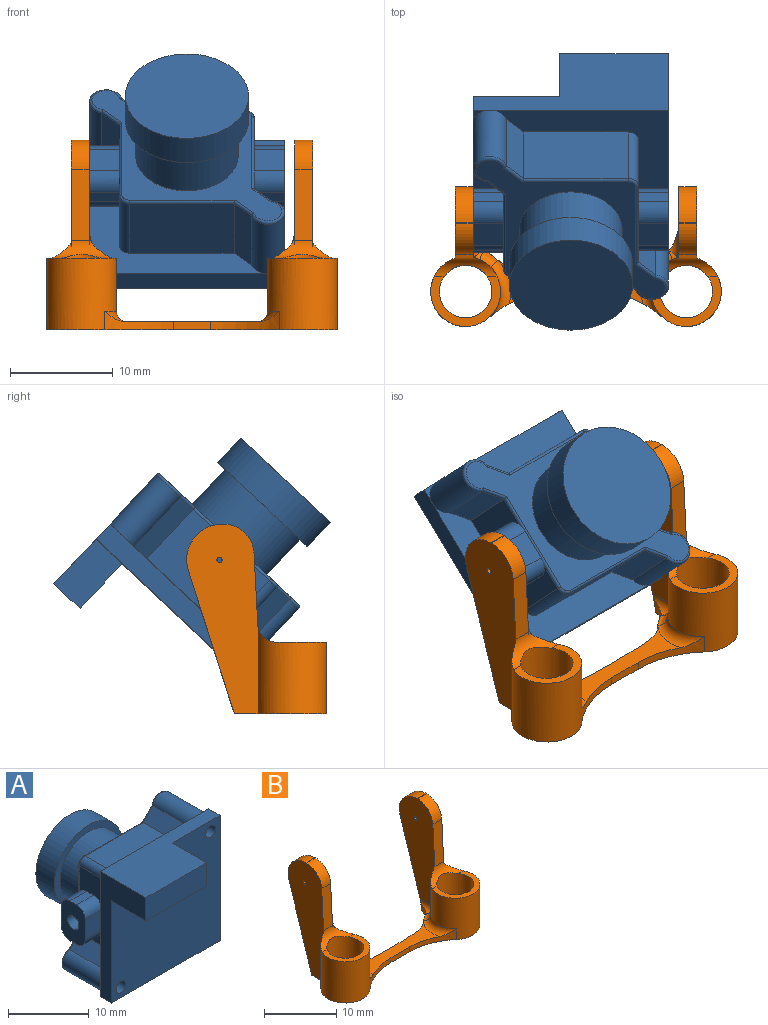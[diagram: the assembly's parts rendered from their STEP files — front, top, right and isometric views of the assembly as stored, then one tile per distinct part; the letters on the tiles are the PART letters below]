
ASSEMBLY  parts=2 mates=1
PART A: 69 faces, bbox 19.3x22.8x19.3 mm
  f0: plane 17.38x17.38mm, normal (0,1,0), area 82.2mm2, adj f3,f4,f43,f59,f60,f61,f62,f63
  f1: plane 1.63x1.63mm, normal (0,1,0), area 0.6mm2, adj f3,f8,f63
  f2: plane 1.63x1.63mm, normal (0,1,0), area 0.6mm2, adj f4,f5,f59
  f3: plane 19x2mm, normal (1,0,0), area 38mm2, adj f0,f1,f4,f8,f10
  f4: plane 19x2mm, normal (0,0,-1), area 38mm2, adj f0,f2,f3,f5,f10
  f5: plane 19x8mm, normal (-1,0,0), area 59mm2, adj f2,f4,f8,f9,f10,f12,f13
  f6: cylinder r=0.88mm len=2mm, axis (0,-1,0), area 11mm2, adj f10,f67
  f7: cylinder r=0.88mm len=2mm, axis (0,-1,0), area 11mm2, adj f10,f68
  f8: plane 19x8mm, normal (0,0,1), area 101.6mm2, adj f1,f3,f5,f9,f10,f11,f13
  f9: plane 17.38x17.38mm, normal (0,1,0), area 82.2mm2, adj f5,f8,f45,f56,f57,f58,f59,f63
  f10: plane 19x19mm, normal (0,-1,0), area 319.1mm2, adj f3,f4,f5,f6,f7,f8,f11,f12
  f11: plane 6x3.5mm, normal (1,0,0), area 21mm2, adj f8,f10,f12,f13
  f12: plane 10.6x6mm, normal (0,0,-1), area 63.6mm2, adj f5,f10,f11,f13
  f13: plane 10.6x3.5mm, normal (0,-1,0), area 37.1mm2, adj f5,f8,f11,f12
  f14: plane 2x2mm, normal (-1,0,0), area 3.1mm2, adj f19
  f15: cylinder r=1.5mm len=2.93mm, axis (-1,0,0), area 6.9mm2, adj f20,f21,f24,f57
  f16: cylinder r=1.5mm len=2.93mm, axis (-1,0,0), area 6.9mm2, adj f20,f22,f24,f25,f57
  f17: cylinder r=1.5mm len=2.93mm, axis (1,0,0), area 6.9mm2, adj f22,f23,f24,f25,f57
  f18: cylinder r=1.5mm len=2.93mm, axis (1,0,0), area 6.9mm2, adj f21,f23,f24,f57
  f19: cylinder r=1mm len=2.93mm, axis (1,0,0), area 18.4mm2, adj f14,f24
  f20: plane 2.93x1.2mm, normal (0,0,1), area 3.5mm2, adj f15,f16,f24,f57
  f21: plane 3x2.93mm, normal (0,-1,0), area 8.8mm2, adj f15,f18,f24,f57
  f22: plane 3x2.93mm, normal (0,1,0), area 8.8mm2, adj f16,f17,f24,f25
  f23: plane 2.93x1.2mm, normal (0,0,-1), area 3.5mm2, adj f17,f18,f24,f57
  f24: plane 6x4.2mm, normal (-1,0,0), area 20.1mm2, adj f15,f16,f17,f18,f19,f20,f21,f22
  f25: plane 4.66x0.25mm, normal (1,0,0), area 1mm2, adj f16,f17,f22,f52
  f26: plane 2x2mm, normal (1,0,0), area 3.1mm2, adj f31
  f27: cylinder r=1.5mm len=2.93mm, axis (1,0,0), area 6.9mm2, adj f32,f33,f36,f66
  f28: cylinder r=1.5mm len=2.93mm, axis (1,0,0), area 6.9mm2, adj f32,f34,f36,f37,f66
  f29: cylinder r=1.5mm len=2.93mm, axis (-1,0,0), area 6.9mm2, adj f34,f35,f36,f37,f66
  f30: cylinder r=1.5mm len=2.93mm, axis (-1,0,0), area 6.9mm2, adj f33,f35,f36,f66
  f31: cylinder r=1mm len=2.93mm, axis (-1,0,0), area 18.4mm2, adj f26,f36
  f32: plane 2.93x1.2mm, normal (0,0,1), area 3.5mm2, adj f27,f28,f36,f66
  f33: plane 3x2.93mm, normal (0,-1,0), area 8.8mm2, adj f27,f30,f36,f66
  f34: plane 3x2.93mm, normal (0,1,0), area 8.8mm2, adj f28,f29,f36,f37
  f35: plane 2.93x1.2mm, normal (0,0,-1), area 3.5mm2, adj f29,f30,f36,f66
  f36: plane 6x4.2mm, normal (1,0,0), area 20.1mm2, adj f27,f28,f29,f30,f31,f32,f33,f34
  f37: plane 4.66x0.25mm, normal (-1,0,0), area 1mm2, adj f28,f29,f34,f49
  f38: plane 12x12mm, normal (0,-1,0), area 34.6mm2, adj f40,f41
  f39: plane 12x12mm, normal (0,1,0), area 113.1mm2, adj f40
  f40: cylinder r=6mm len=12mm, axis (0,-1,0), area 121.8mm2, adj f38,f39
  f41: cylinder r=5mm len=10mm, axis (0,-1,0), area 148.3mm2, adj f38,f65
  f42: torus R=0.75mm, axis (0,1,0), area 0.6mm2, adj f43,f47,f49,f65
  f43: cylinder r=1mm len=6.6mm, axis (0,-1,0), area 10.4mm2, adj f0,f42,f61,f66
  f44: torus R=0.75mm, axis (0,1,0), area 0.6mm2, adj f45,f52,f54,f65
  f45: cylinder r=1mm len=6.6mm, axis (0,-1,0), area 10.4mm2, adj f9,f44,f56,f57
  f46: cylinder r=0.25mm len=2.01mm, axis (0.71,0,0.71), area 1mm2, adj f47,f48,f60,f65
  f47: cylinder r=0.25mm len=10.27mm, axis (1,0,0), area 4mm2, adj f42,f46,f61,f65
  f48: torus R=1.38mm, axis (0,1,0), area 2.6mm2, adj f46,f50,f59,f65
  f49: cylinder r=0.25mm len=10.27mm, axis (0,0,1), area 4mm2, adj f37,f42,f51,f65,f66
  f50: cylinder r=0.25mm len=2.01mm, axis (-0.71,0,-0.71), area 1mm2, adj f48,f52,f58,f65
  f51: cylinder r=0.25mm len=2.01mm, axis (0.71,0,0.71), area 1mm2, adj f49,f53,f62,f65
  f52: cylinder r=0.25mm len=10.27mm, axis (0,0,-1), area 4mm2, adj f25,f44,f50,f57,f65
  f53: torus R=1.38mm, axis (0,1,0), area 2.6mm2, adj f51,f55,f63,f65
  f54: cylinder r=0.25mm len=10.27mm, axis (-1,0,0), area 4mm2, adj f44,f55,f56,f65
  f55: cylinder r=0.25mm len=2.01mm, axis (-0.71,0,-0.71), area 1mm2, adj f53,f54,f64,f65
  f56: plane 10.17x6.6mm, normal (0,0,1), area 67.1mm2, adj f9,f45,f54,f64
  f57: plane 10.17x6.6mm, normal (-1,0,0), area 44.9mm2, adj f9,f15,f16,f17,f18,f20,f21,f23
  f58: plane 6.6x1.71mm, normal (-0.71,0,0.71), area 15.9mm2, adj f9,f50,f57,f59
  f59: cylinder r=1.62mm len=6.6mm, axis (0,-1,0), area 45.1mm2, adj f0,f2,f9,f48,f58,f60
  f60: plane 6.6x1.71mm, normal (0.71,0,-0.71), area 15.9mm2, adj f0,f46,f59,f61
  f61: plane 10.17x6.6mm, normal (0,0,-1), area 67.1mm2, adj f0,f43,f47,f60
  f62: plane 6.6x1.71mm, normal (0.71,0,-0.71), area 15.9mm2, adj f0,f51,f63,f66
  f63: cylinder r=1.62mm len=6.6mm, axis (0,-1,0), area 45.1mm2, adj f0,f1,f9,f53,f62,f64
  f64: plane 6.6x1.71mm, normal (-0.71,0,0.71), area 15.9mm2, adj f9,f55,f56,f63
  f65: plane 18.5x18.5mm, normal (0,1,0), area 100.4mm2, adj f41,f42,f44,f46,f47,f48,f49,f50
  f66: plane 10.17x6.6mm, normal (1,0,0), area 44.9mm2, adj f0,f27,f28,f29,f30,f32,f33,f35
  f67: plane 1.75x1.75mm, normal (0,-1,0), area 2.4mm2, adj f6
  f68: plane 1.75x1.75mm, normal (0,-1,0), area 2.4mm2, adj f7
PART B: 41 faces, bbox 28.3x14.4x18.5 mm
  f0: plane 28.3x9.08mm, normal (0,0,-1), area 81.9mm2, adj f1,f4,f6,f8,f9,f12,f14,f21
  f1: extruded ~9.97x4.33mm, area 9.7mm2, adj f0,f2,f4,f5,f30,f32,f35
  f2: cylinder r=1mm len=2.82mm, axis (0,1,0), area 2.5mm2, adj f1,f25,f30,f32,f34
  f3: cylinder r=1mm len=2.82mm, axis (0,1,0), area 2.5mm2, adj f4,f7,f12,f15,f17
  f4: extruded ~9.97x4.33mm, area 9.7mm2, adj f0,f1,f3,f5,f12,f15,f18
  f5: plane 15.44x4.35mm, normal (0,0,1), area 27.6mm2, adj f1,f4,f14,f19,f21,f36,f38
  f6: cylinder r=3.4mm len=9.51mm, axis (0,0,-1), area 127mm2, adj f0,f7,f9,f10,f11,f17,f18,f19
  f7: plane 16.7x6.89mm, normal (1,0,0), area 82.6mm2, adj f3,f6,f11,f12,f13,f16,f22,f23
  f8: cylinder r=2.56mm len=7.36mm, axis (0,0,-1), area 113.5mm2, adj f0,f10,f20
  f9: plane 18.5x6.95mm, normal (-1,0,0), area 87.7mm2, adj f0,f6,f11,f12,f13,f16,f20,f22
  f10: plane 6.8x4.88mm, normal (0,0,1), area 10.5mm2, adj f6,f8,f20
  f11: plane 6.99x1.96mm, normal (0,-1,0.05), area 12.3mm2, adj f6,f7,f9,f16,f20
  f12: plane 13.94x4.48mm, normal (0,0.95,-0.31), area 25.8mm2, adj f0,f3,f4,f7,f9,f22
  f13: plane 1.75x0.08mm, normal (0,0,1), area 0.1mm2, adj f7,f9,f16,f22
  f14: plane 3.66x0.8mm, normal (0,-1,0), area 2.9mm2, adj f0,f5,f21,f38
  f15: plane 0.01x0.01mm, normal (0,0,1), area 0mm2, adj f3,f4,f17
  f16: cylinder r=3mm len=3mm, axis (-1,0,0), area 8mm2, adj f7,f9,f11,f13
  f17: torus R=4.4mm, axis (0,0,1), area 0.7mm2, adj f3,f6,f15,f18
  f18: bspline ~2.01x1.83mm, area 2.3mm2, adj f4,f6,f17,f19
  f19: torus R=4.4mm, axis (0,0,1), area 7.6mm2, adj f5,f6,f18,f21
  f20: cylinder r=1.8mm len=6.13mm, axis (1,0,0), area 7.6mm2, adj f6,f8,f9,f10,f11
  f21: cylinder r=10mm len=6.66mm, axis (0,0,-1), area 6.7mm2, adj f0,f5,f6,f14,f19
  f22: cylinder r=3.49mm len=4.56mm, axis (-1,0,0), area 11.5mm2, adj f7,f9,f12,f13
  f23: cylinder r=0.25mm len=1.75mm, axis (1,0,0), area 2.7mm2, adj f7,f9
  f24: cylinder r=3.4mm len=9.51mm, axis (0,0,-1), area 127mm2, adj f0,f25,f27,f28,f29,f34,f35,f36
  f25: plane 16.7x6.89mm, normal (-1,0,0), area 82.6mm2, adj f2,f24,f29,f30,f31,f33,f39,f40
  f26: cylinder r=2.56mm len=7.36mm, axis (0,0,-1), area 113.5mm2, adj f0,f28,f37
  f27: plane 18.5x6.95mm, normal (1,0,0), area 87.7mm2, adj f0,f24,f29,f30,f31,f33,f37,f39
  f28: plane 6.8x4.88mm, normal (0,0,1), area 10.5mm2, adj f24,f26,f37
  f29: plane 6.99x1.96mm, normal (0,-1,0.05), area 12.3mm2, adj f24,f25,f27,f33,f37
  f30: plane 13.94x4.48mm, normal (0,0.95,-0.31), area 25.8mm2, adj f0,f1,f2,f25,f27,f39
  f31: plane 1.75x0.08mm, normal (0,0,1), area 0.1mm2, adj f25,f27,f33,f39
  f32: plane 0.01x0.01mm, normal (0,0,1), area 0mm2, adj f1,f2,f34
  f33: cylinder r=3mm len=3mm, axis (1,0,0), area 8mm2, adj f25,f27,f29,f31
  f34: torus R=4.4mm, axis (0,0,1), area 0.7mm2, adj f2,f24,f32,f35
  f35: bspline ~2.01x1.83mm, area 2.3mm2, adj f1,f24,f34,f36
  f36: torus R=4.4mm, axis (0,0,1), area 7.6mm2, adj f5,f24,f35,f38
  f37: cylinder r=1.8mm len=6.13mm, axis (-1,0,0), area 7.6mm2, adj f24,f26,f27,f28,f29
  f38: cylinder r=10mm len=6.66mm, axis (0,0,-1), area 6.7mm2, adj f0,f5,f14,f24,f36
  f39: cylinder r=3.49mm len=4.56mm, axis (1,0,0), area 11.5mm2, adj f25,f27,f30,f31
  f40: cylinder r=0.25mm len=1.75mm, axis (-1,0,0), area 2.7mm2, adj f25,f27
PLACE A rot(axis=(0,-0.4,-0.92),180deg) t=(-0.5,11.3,9.73)mm
PLACE B t=(0,-0.81,-0.8)mm
MATE revolute A.f19 <-> B.f23  axis (1,0,0) through (-10,6.19,14.2)mm
